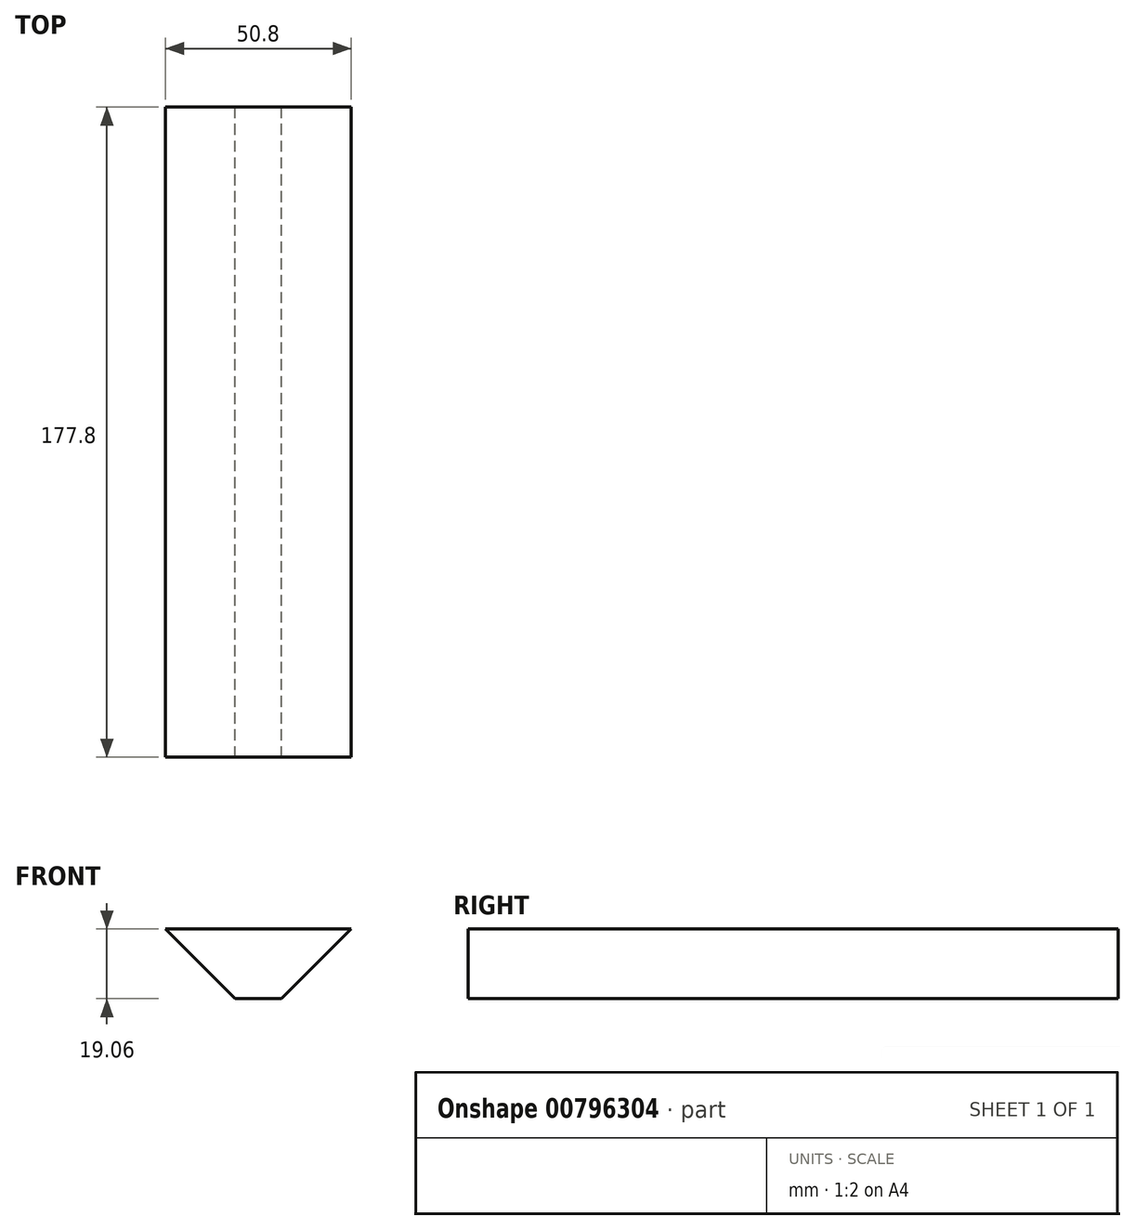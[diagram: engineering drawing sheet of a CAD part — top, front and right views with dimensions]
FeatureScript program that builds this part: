
annotation { "Feature Type Name" : "Feature", "Feature Type Description" : "" }
export const myFeature = defineFeature(function(context is Context, id is Id, definition is map)
    precondition{}
    {
        {
            var Q0;
            Q0=qCreatedBy(makeId("Front.planeOp"),FACE);
            var sketch = newSketch(context, id + "F0", { "sketchPlane" : qUnion([Q0])});
            skLineSegment(sketch, "E0.bottom", {"start": v(-25.4, 9.53) * mm, "end": v(25.4, 9.53) * mm});
            skLineSegment(sketch, "E0.top", {"start": v(-25.4, -9.52) * mm, "end": v(25.4, -9.52) * mm});
            skLineSegment(sketch, "E0.left", {"start": v(-25.4, 9.53) * mm, "end": v(-25.4, -9.52) * mm});
            skLineSegment(sketch, "E0.right", {"start": v(25.4, 9.53) * mm, "end": v(25.4, -9.52) * mm});
            skPoint(sketch, "E0.middle", {"position": v(0, 0) * mm});
            skLineSegment(sketch, "E1", {"start": v(-25.4, 9.53) * mm, "end": v(-6.35, -9.52) * mm});
            skLineSegment(sketch, "E2", {"start": v(25.4, 9.53) * mm, "end": v(6.35, -9.52) * mm});
            skSolve(sketch);
        }
        {
            var Q0;
            Q0=makeQuery(id+"F0.imprint","IMPRINT",FACE,{"disambiguationData":[TD([[makeQuery(id+"F0.imprint","IMPRINT",EDGE,{"derivedFrom":sQuery(id+"F0.wireOp",EDGE,"E0.bottom")}),-1.0]])]});
            extrude(context, id + "F1", {"entities" : qUnion([Q0]), "endBound" : BoundingType.SYMMETRIC, "depth" : 177.8 * mm, "offsetDistance" : 25.4 * mm});
        }
    });
